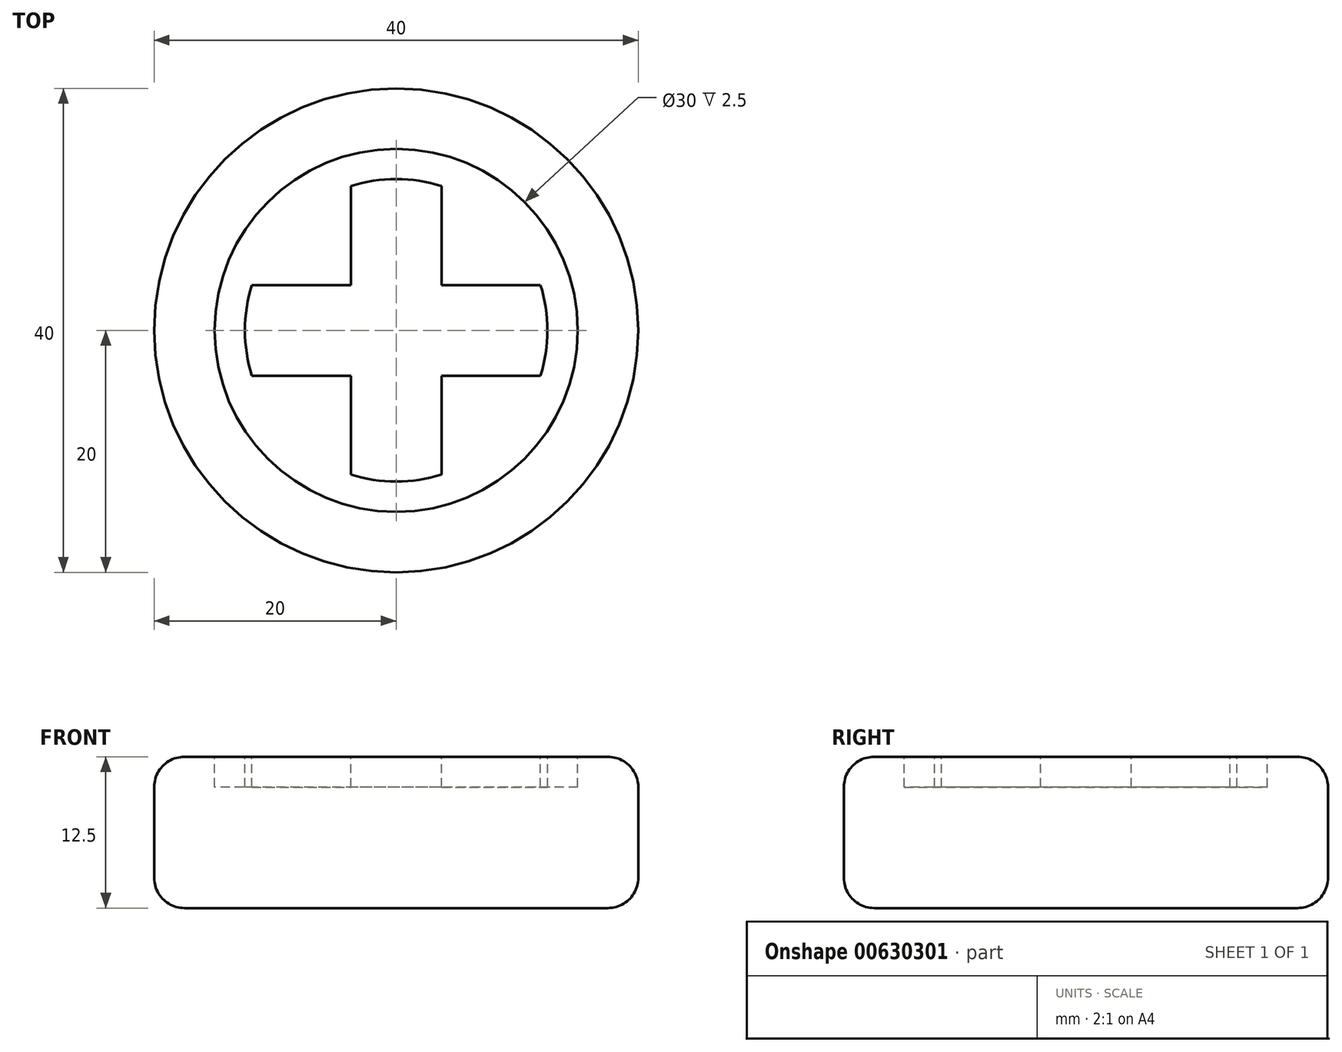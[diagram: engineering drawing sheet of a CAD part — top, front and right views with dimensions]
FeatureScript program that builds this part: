
annotation { "Feature Type Name" : "Feature", "Feature Type Description" : "" }
export const myFeature = defineFeature(function(context is Context, id is Id, definition is map)
    precondition{}
    {
        {
            var Q0;
            Q0=qCreatedBy(makeId("Top.planeOp"),FACE);
            var sketch = newSketch(context, id + "F0", { "sketchPlane" : qUnion([Q0])});
            skCircle(sketch, "E0", {"center": v(0, 0) * mm, "radius": 20 * mm});
            skSolve(sketch);
        }
        {
            var Q0;
            Q0 = qSketchRegion(id + "F0", true);
            extrude(context, id + "F1", {"entities" : qUnion([Q0]), "depth" : 12.5 * mm, "offsetDistance" : 25 * mm});
        }
        {
            var Q0;
            Q0=makeQuery(id+"F1.opExtrude","CAP_EDGE",EDGE,{"disambiguationData":[OSD([sQuery(id+"F0.wireOp",EDGE,"E0")])],"isStart":false});
            fillet(context, id + "F2", {"entities" : qUnion([Q0]), "radius" : 2.5 * mm, "tangentPropagation" : true, "allowEdgeOverflow" : false});
        }
        {
            var Q0;
            Q0=makeQuery(id+"F1.opExtrude","CAP_EDGE",EDGE,{"disambiguationData":[OSD([sQuery(id+"F0.wireOp",EDGE,"E0")])],"isStart":true});
            fillet(context, id + "F3", {"entities" : qUnion([Q0]), "radius" : 2.5 * mm, "tangentPropagation" : true, "allowEdgeOverflow" : false});
        }
        {
            var Q0;
            Q0=makeQuery(id+"F1.opExtrude","CAP_FACE",FACE,{"disambiguationData":[OSD([sQuery(id+"F0.wireOp",EDGE,"E0")])],"isStart":false});
            var sketch = newSketch(context, id + "F4", { "sketchPlane" : qUnion([Q0])});
            skCircle(sketch, "E1", {"center": v(0, 0) * mm, "radius": 15 * mm});
            skLineSegment(sketch, "E2.left", {"start": v(-3.75, 11.92) * mm, "end": v(-3.75, 3.75) * mm});
            skLineSegment(sketch, "E2.right", {"start": v(3.75, 11.92) * mm, "end": v(3.75, 3.75) * mm});
            skArc(sketch, "E3", {"start": v(3.75, 11.92) * mm, "mid": v(0, 12.5) * mm, "end": v(-3.75, 11.92) * mm});
            skLineSegment(sketch, "E4.trimOffspring", {"start": v(-11.92, -3.75) * mm, "end": v(-3.75, -3.75) * mm});
            skLineSegment(sketch, "E5.trimOffspring", {"start": v(-11.92, 3.75) * mm, "end": v(-3.75, 3.75) * mm});
            skArc(sketch, "E6.trimOffspring", {"start": v(-11.92, 3.75) * mm, "mid": v(-12.5, 0) * mm, "end": v(-11.92, -3.75) * mm});
            skArc(sketch, "E7.trimOffspring", {"start": v(-3.75, -11.92) * mm, "mid": v(0, -12.5) * mm, "end": v(3.75, -11.92) * mm});
            skArc(sketch, "E8.trimOffspring", {"start": v(11.92, -3.75) * mm, "mid": v(12.5, 0) * mm, "end": v(11.92, 3.75) * mm});
            skLineSegment(sketch, "E9.trimOffspring", {"start": v(3.75, -3.75) * mm, "end": v(3.75, -11.92) * mm});
            skLineSegment(sketch, "E10.trimOffspring", {"start": v(3.75, -3.75) * mm, "end": v(11.92, -3.75) * mm});
            skLineSegment(sketch, "E11.trimOffspring", {"start": v(-3.75, -3.75) * mm, "end": v(-3.75, -11.92) * mm});
            skLineSegment(sketch, "E12.trimOffspring", {"start": v(3.75, 3.75) * mm, "end": v(11.92, 3.75) * mm});
            skSolve(sketch);
        }
        {
            var Q0;
            Q0=makeQuery(id+"F4.imprint","IMPRINT",FACE,{"disambiguationData":[TD([[makeQuery(id+"F4.imprint","IMPRINT",EDGE,{"derivedFrom":sQuery(id+"F4.wireOp",EDGE,"E1")}),1.0]])]});
            extrude(context, id + "F5", {"entities" : qUnion([Q0]), "operationType" : NewBodyOperationType.REMOVE, "oppositeDirection" : true, "depth" : 2.5 * mm, "offsetDistance" : 25 * mm});
        }
    });
